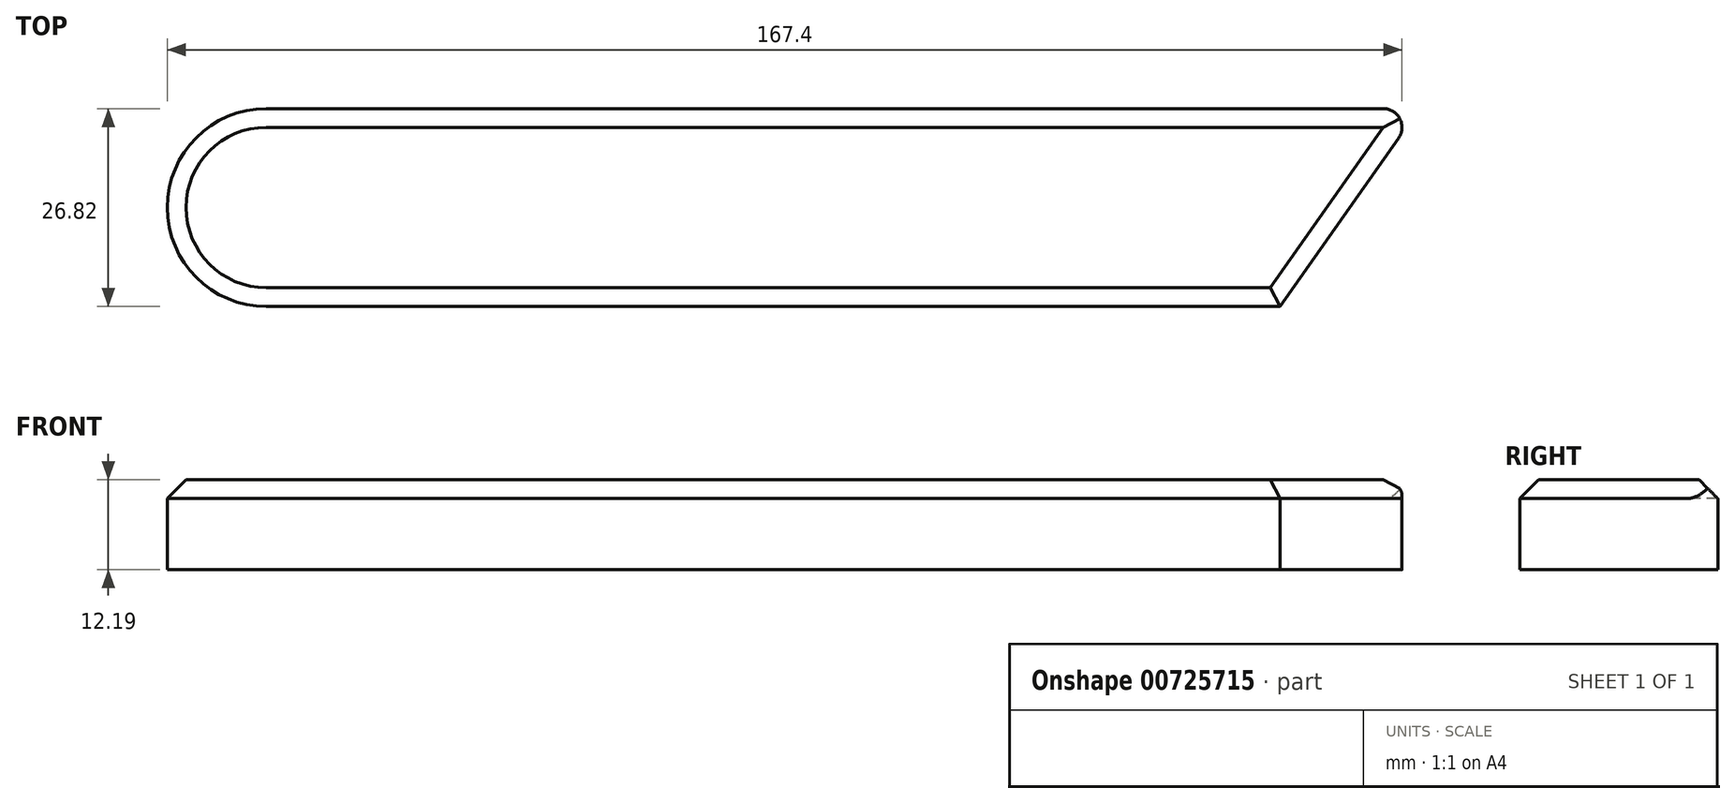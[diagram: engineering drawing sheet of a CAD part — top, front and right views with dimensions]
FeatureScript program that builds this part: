
annotation { "Feature Type Name" : "Feature", "Feature Type Description" : "" }
export const myFeature = defineFeature(function(context is Context, id is Id, definition is map)
    precondition{}
    {
        {
            var Q0;
            Q0=qCreatedBy(makeId("Top.planeOp"),FACE);
            var sketch = newSketch(context, id + "F0", { "sketchPlane" : qUnion([Q0])});
            skLineSegment(sketch, "E0.bottom", {"start": v(68.74, 13.41) * mm, "end": v(-68.74, 13.41) * mm});
            skLineSegment(sketch, "E0.top", {"start": v(68.74, -13.41) * mm, "end": v(-68.74, -13.41) * mm});
            skLineSegment(sketch, "E0.left", {"start": v(68.74, 13.41) * mm, "end": v(68.74, -13.41) * mm});
            skLineSegment(sketch, "E0.right", {"start": v(-68.74, 13.41) * mm, "end": v(-68.74, -13.41) * mm});
            skPoint(sketch, "E0.middle", {"position": v(0, 0) * mm});
            skLineSegment(sketch, "E1", {"start": v(68.74, 13.41) * mm, "end": v(87.6, 13.41) * mm});
            skLineSegment(sketch, "E2", {"start": v(87.6, 13.41) * mm, "end": v(68.74, -13.41) * mm});
            skArc(sketch, "E3", {"start": v(-68.74, 13.41) * mm, "mid": v(-82.15, 0) * mm, "end": v(-68.74, -13.41) * mm});
            skSolve(sketch);
        }
        {
            var Q0;
            Q0=makeQuery(id+"F0.imprint","IMPRINT",FACE,{"disambiguationData":[TD([[makeQuery(id+"F0.imprint","IMPRINT",EDGE,{"derivedFrom":sQuery(id+"F0.wireOp",EDGE,"E0.right")}),-1.0]])]});
            var Q1;
            Q1=makeQuery(id+"F0.imprint","IMPRINT",FACE,{"disambiguationData":[TD([[makeQuery(id+"F0.imprint","IMPRINT",EDGE,{"derivedFrom":sQuery(id+"F0.wireOp",EDGE,"E0.bottom")}),1.0]])]});
            var Q2;
            Q2=makeQuery(id+"F0.imprint","IMPRINT",FACE,{"disambiguationData":[TD([[makeQuery(id+"F0.imprint","IMPRINT",EDGE,{"derivedFrom":sQuery(id+"F0.wireOp",EDGE,"E0.left")}),1.0]])]});
            extrude(context, id + "F1", {"entities" : qUnion([Q0, Q1, Q2]), "depth" : 12.2 * mm, "offsetDistance" : 25.4 * mm});
        }
        {
            var Q0;
            Q0=makeQuery(id+"F1.opExtrude","CAP_EDGE",EDGE,{"disambiguationData":[OSD([sQuery(id+"F0.wireOp",EDGE,"E0.bottom"),sQuery(id+"F0.wireOp",EDGE,"E1")])],"isStart":false});
            var Q1;
            Q1=makeQuery(id+"F1.opExtrude","CAP_EDGE",EDGE,{"disambiguationData":[OSD([sQuery(id+"F0.wireOp",EDGE,"E3")])],"isStart":false});
            var Q2;
            Q2=makeQuery(id+"F1.opExtrude","CAP_EDGE",EDGE,{"disambiguationData":[OSD([sQuery(id+"F0.wireOp",EDGE,"E0.top")])],"isStart":false});
            var Q3;
            Q3=makeQuery(id+"F1.opExtrude","CAP_EDGE",EDGE,{"disambiguationData":[OSD([sQuery(id+"F0.wireOp",EDGE,"E2")])],"isStart":false});
            chamfer(context, id + "F2", {"entities" : qUnion([Q0, Q1, Q2, Q3]), "width" : 2.54 * mm, "tangentPropagation" : true});
        }
        {
            var Q0;
            Q0=makeQuery(id+"F1.opExtrude","SWEPT_EDGE",EDGE,{"disambiguationData":[OSD([sQuery(id+"F0.wireOp",EDGE,"E1"),sQuery(id+"F0.wireOp",EDGE,"E2")])]});
            fillet(context, id + "F3", {"entities" : qUnion([Q0]), "radius" : 2.54 * mm, "tangentPropagation" : true, "allowEdgeOverflow" : false});
        }
    });
